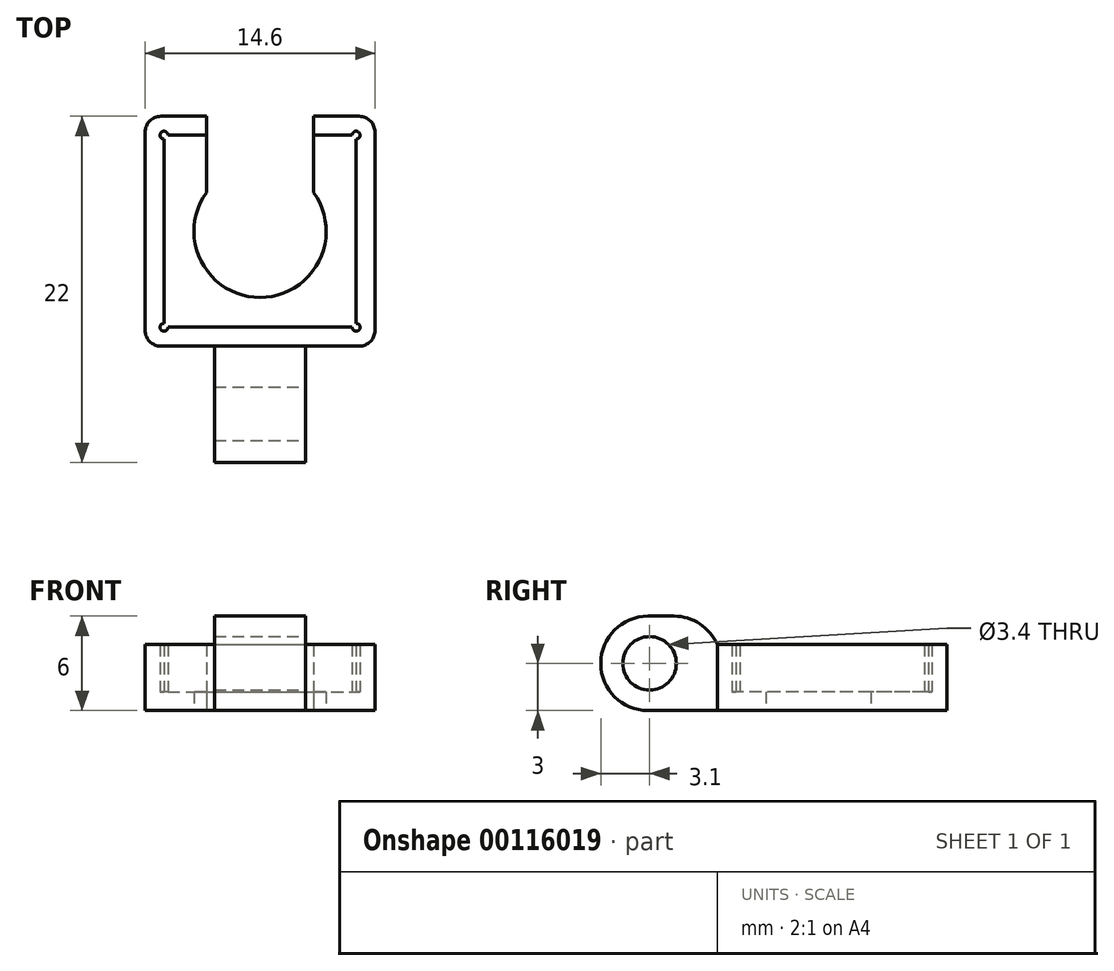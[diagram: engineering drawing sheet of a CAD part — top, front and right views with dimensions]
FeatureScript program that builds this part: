
annotation { "Feature Type Name" : "Feature", "Feature Type Description" : "" }
export const myFeature = defineFeature(function(context is Context, id is Id, definition is map)
    precondition{}
    {
        {
            var Q0;
            Q0=qCreatedBy(makeId("Top.planeOp"),FACE);
            var sketch = newSketch(context, id + "F0", { "sketchPlane" : qUnion([Q0])});
            skLineSegment(sketch, "E0.bottom", {"start": v(-5.85, 6.1) * mm, "end": v(-3.4, 6.1) * mm});
            skLineSegment(sketch, "E0.top", {"start": v(-5.85, -6.1) * mm, "end": v(5.85, -6.1) * mm});
            skLineSegment(sketch, "E0.left", {"start": v(-6.1, 5.85) * mm, "end": v(-6.1, -5.85) * mm});
            skLineSegment(sketch, "E0.right", {"start": v(6.1, 5.85) * mm, "end": v(6.1, -5.85) * mm});
            skLineSegment(sketch, "E1.0", {"start": v(-7.3, 7.3) * mm, "end": v(-3.4, 7.3) * mm});
            skLineSegment(sketch, "E1.1", {"start": v(-7.3, 7.3) * mm, "end": v(-7.3, -7.3) * mm});
            skLineSegment(sketch, "E1.2", {"start": v(-7.3, -7.3) * mm, "end": v(7.3, -7.3) * mm});
            skLineSegment(sketch, "E1.3", {"start": v(7.3, 7.3) * mm, "end": v(7.3, -7.3) * mm});
            skArc(sketch, "E2", {"start": v(-3.4, 2.47) * mm, "mid": v(0, -4.2) * mm, "end": v(3.4, 2.47) * mm});
            skLineSegment(sketch, "E3", {"start": v(-3.4, 7.3) * mm, "end": v(-3.4, 2.47) * mm});
            skLineSegment(sketch, "E4.MirrorCS", {"start": v(3.4, 7.3) * mm, "end": v(3.4, 2.47) * mm});
            skLineSegment(sketch, "E5.trimOffspring", {"start": v(3.4, 7.3) * mm, "end": v(7.3, 7.3) * mm});
            skLineSegment(sketch, "E6.trimOffspring", {"start": v(3.4, 6.1) * mm, "end": v(5.85, 6.1) * mm});
            skLineSegment(sketch, "E7.top", {"start": v(-2.9, -14.7) * mm, "end": v(0, -14.7) * mm});
            skLineSegment(sketch, "E7.left", {"start": v(-2.9, -7.3) * mm, "end": v(-2.9, -14.7) * mm});
            skLineSegment(sketch, "E8.MirrorCS", {"start": v(2.9, -14.7) * mm, "end": v(0, -14.7) * mm});
            skLineSegment(sketch, "E9.MirrorCS", {"start": v(2.9, -7.3) * mm, "end": v(2.9, -14.7) * mm});
            skArc(sketch, "E10", {"start": v(-5.85, 6.1) * mm, "mid": v(-6.28, 6.28) * mm, "end": v(-6.1, 5.85) * mm});
            skArc(sketch, "E11.MirrorCS", {"start": v(5.85, 6.1) * mm, "mid": v(6.28, 6.28) * mm, "end": v(6.1, 5.85) * mm});
            skArc(sketch, "E12.MirrorCS", {"start": v(5.85, -6.1) * mm, "mid": v(6.28, -6.28) * mm, "end": v(6.1, -5.85) * mm});
            skArc(sketch, "E13.MirrorCS", {"start": v(-5.85, -6.1) * mm, "mid": v(-6.28, -6.28) * mm, "end": v(-6.1, -5.85) * mm});
            skSolve(sketch);
        }
        {
            var Q0;
            {var subQ1=sQuery(id+"F0.wireOp",EDGE,"E0.bottom");Q0=makeQuery(id+"F0.imprint","IMPRINT",FACE,{"disambiguationData":[TD([[makeQuery(id+"F0.imprint","IMPRINT",EDGE,{"derivedFrom":subQ1}),-1.0]])]});}
            extrude(context, id + "F1", {"entities" : qUnion([Q0]), "depth" : 1.2 * mm});
        }
        {
            var Q0;
            {var subQ3=sQuery(id+"F0.wireOp",EDGE,"E0.bottom");Q0=makeQuery(id+"F0.imprint","IMPRINT",FACE,{"disambiguationData":[TD([[makeQuery(id+"F0.imprint","IMPRINT",EDGE,{"derivedFrom":subQ3}),1.0]])]});}
            extrude(context, id + "F2", {"entities" : qUnion([Q0]), "operationType" : NewBodyOperationType.ADD, "depth" : 4.2 * mm});
        }
        {
            var Q0;
            Q0=makeQuery(id+"F0.imprint","IMPRINT",FACE,{"disambiguationData":[TD([[makeQuery(id+"F0.imprint","IMPRINT",EDGE,{"derivedFrom":sQuery(id+"F0.wireOp",EDGE,"E7.top")}),1.0]])]});
            extrude(context, id + "F3", {"entities" : qUnion([Q0]), "operationType" : NewBodyOperationType.ADD, "depth" : 6 * mm});
        }
        {
            var Q0;
            Q0=qCreatedBy(makeId("Right.planeOp"),FACE);
            cPlane(context, id + "F4", {"entities" : qUnion([Q0]), "cplaneType" : CPlaneType.OFFSET, "offset" : 3 * mm, "width" : 150 * mm, "height" : 150 * mm});
        }
        {
            var Q0;
            Q0=qCreatedBy(id+"F4.planeOp",FACE);
            var sketch = newSketch(context, id + "F5", { "sketchPlane" : qUnion([Q0])});
            skCircle(sketch, "E14", {"center": v(-11.6, 3) * mm, "radius": 1.7 * mm});
            skSolve(sketch);
        }
        {
            var Q0;
            Q0=makeQuery(id+"F3.opExtrude","CAP_EDGE",EDGE,{"disambiguationData":[OSD([sQuery(id+"F0.wireOp",EDGE,"E7.top"),sQuery(id+"F0.wireOp",EDGE,"E8.MirrorCS")])],"isStart":true});
            var Q1;
            Q1=makeQuery(id+"F3.opExtrude","CAP_EDGE",EDGE,{"disambiguationData":[OSD([sQuery(id+"F0.wireOp",EDGE,"E7.top"),sQuery(id+"F0.wireOp",EDGE,"E8.MirrorCS")])],"isStart":false});
            var Q2;
            Q2=makeQuery(id+"F3.opExtrude","CAP_EDGE",EDGE,{"disambiguationData":[OSD([sQuery(id+"F0.wireOp",EDGE,"E1.2")])],"isStart":false});
            fillet(context, id + "F6", {"entities" : qUnion([Q0, Q1, Q2]), "radius" : 3 * mm, "tangentPropagation" : true, "allowEdgeOverflow" : false});
        }
        {
            var Q0;
            Q0=sQuery(id+"F5.wireOp",VERTEX,"E14.center");
            var Q1;
            Q1=makeQuery(id+"F1.opExtrude","SWEPT_BODY",BODY,{"disambiguationData":[OSD([sQuery(id+"F0.wireOp",EDGE,"E0.bottom"),sQuery(id+"F0.wireOp",EDGE,"E0.top"),sQuery(id+"F0.wireOp",EDGE,"E0.left"),sQuery(id+"F0.wireOp",EDGE,"E0.right"),sQuery(id+"F0.wireOp",EDGE,"E2"),sQuery(id+"F0.wireOp",EDGE,"E3"),sQuery(id+"F0.wireOp",EDGE,"E4.MirrorCS"),sQuery(id+"F0.wireOp",EDGE,"E6.trimOffspring")])]});
            hole(context, id + "F7", {"style" : HoleStyle.SIMPLE, "endStyle" : HoleEndStyle.BLIND, "holeDiameter" : 3.4 * mm, "holeDepth" : 7 * mm, "startFromSketch" : true, "locations" : qUnion([Q0]), "scope" : qUnion([Q1])});
        }
        {
            var Q0;
            Q0=makeQuery(id+"F2.opExtrude","SWEPT_EDGE",EDGE,{"disambiguationData":[OSD([sQuery(id+"F0.wireOp",EDGE,"E1.0"),sQuery(id+"F0.wireOp",EDGE,"E1.1")])]});
            var Q1;
            Q1=makeQuery(id+"F2.opExtrude","SWEPT_EDGE",EDGE,{"disambiguationData":[OSD([sQuery(id+"F0.wireOp",EDGE,"E1.1"),sQuery(id+"F0.wireOp",EDGE,"E1.2")])]});
            var Q2;
            Q2=makeQuery(id+"F2.opExtrude","SWEPT_EDGE",EDGE,{"disambiguationData":[OSD([sQuery(id+"F0.wireOp",EDGE,"E1.3"),sQuery(id+"F0.wireOp",EDGE,"E5.trimOffspring")])]});
            var Q3;
            Q3=makeQuery(id+"F2.opExtrude","SWEPT_EDGE",EDGE,{"disambiguationData":[OSD([sQuery(id+"F0.wireOp",EDGE,"E1.2"),sQuery(id+"F0.wireOp",EDGE,"E1.3")])]});
            fillet(context, id + "F8", {"entities" : qUnion([Q0, Q1, Q2, Q3]), "radius" : 1 * mm, "tangentPropagation" : true, "allowEdgeOverflow" : false});
        }
    });
